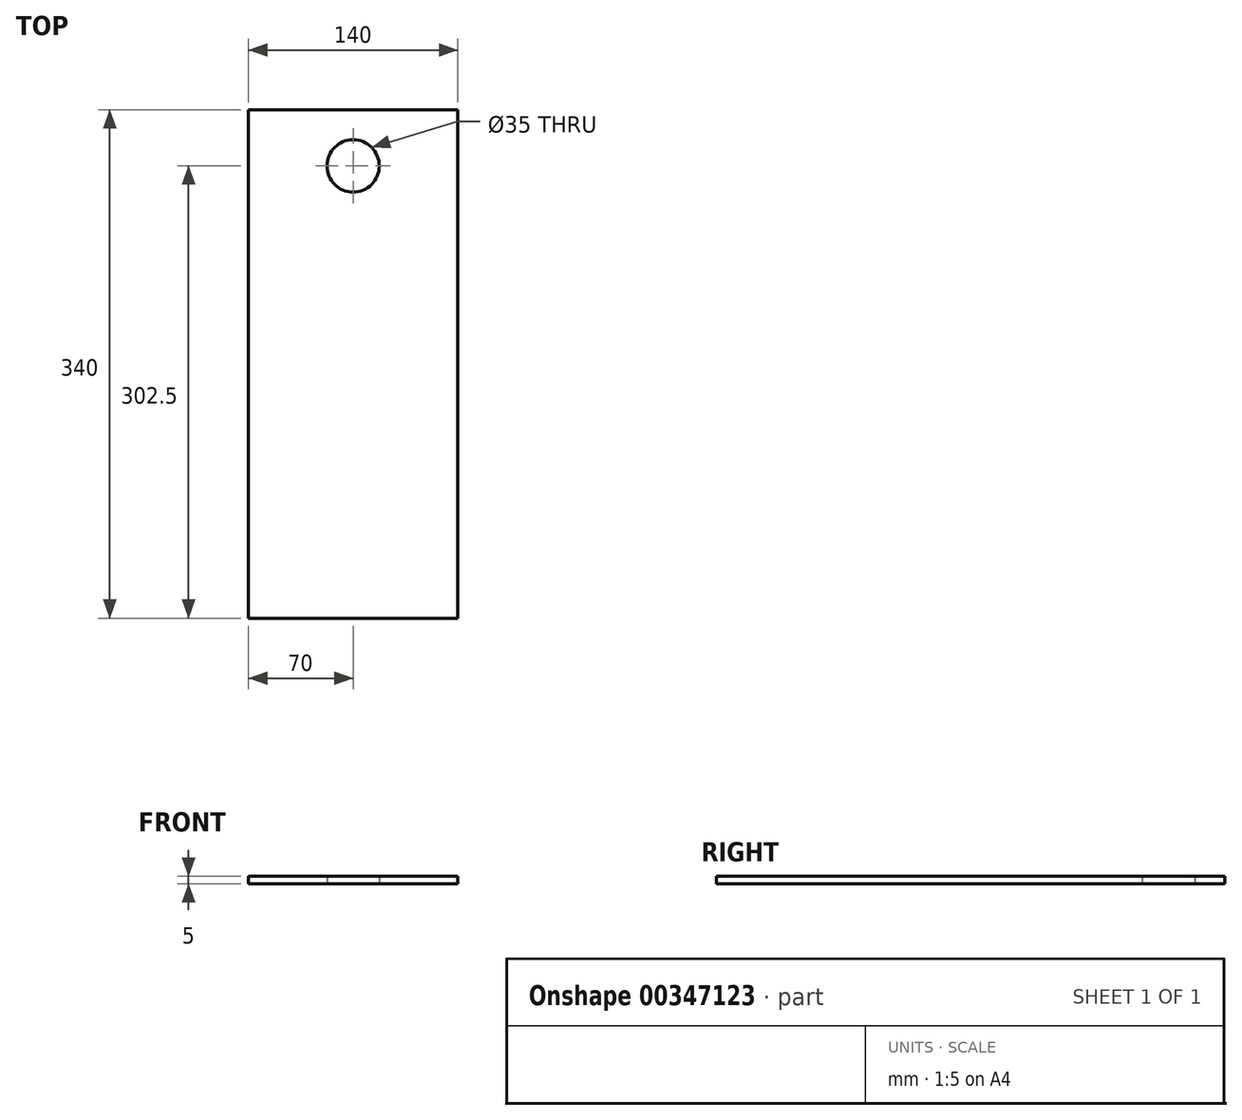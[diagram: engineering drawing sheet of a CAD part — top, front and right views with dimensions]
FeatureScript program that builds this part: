
annotation { "Feature Type Name" : "Feature", "Feature Type Description" : "" }
export const myFeature = defineFeature(function(context is Context, id is Id, definition is map)
    precondition{}
    {
        {
            var Q0;
            Q0=qCreatedBy(makeId("Top.planeOp"),FACE);
            var sketch = newSketch(context, id + "F0", { "sketchPlane" : qUnion([Q0])});
            skLineSegment(sketch, "E0.bottom", {"start": v(-70, 170) * mm, "end": v(70, 170) * mm});
            skLineSegment(sketch, "E0.left", {"start": v(-70, 170) * mm, "end": v(-70, -170) * mm});
            skLineSegment(sketch, "E0.right", {"start": v(70, 170) * mm, "end": v(70, -170) * mm});
            skPoint(sketch, "E0.middle", {"position": v(0, 0) * mm});
            skLineSegment(sketch, "E1", {"start": v(-70, -170) * mm, "end": v(70, -170) * mm});
            skCircle(sketch, "E2", {"center": v(0, 132.5) * mm, "radius": 17.5 * mm});
            skSolve(sketch);
        }
        {
            var Q0;
            Q0=qSketchRegion(id+"F0",true);
            extrude(context, id + "F1", {"entities" : qUnion([Q0]), "depth" : 5 * mm});
        }
    });
